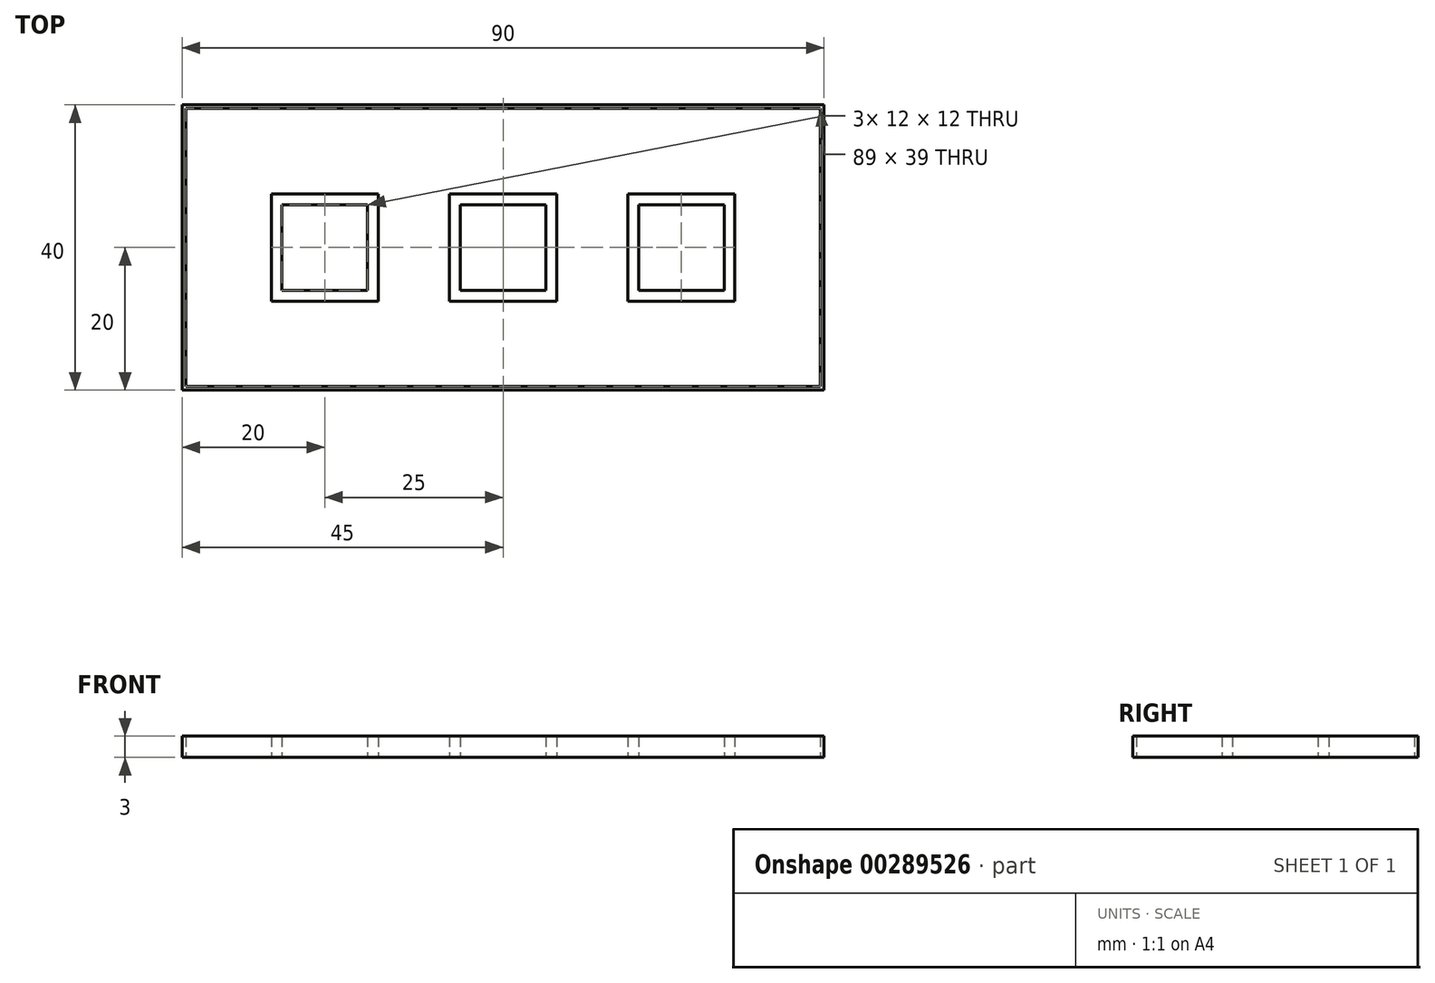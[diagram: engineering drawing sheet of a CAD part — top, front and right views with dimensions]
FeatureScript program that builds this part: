
annotation { "Feature Type Name" : "Feature", "Feature Type Description" : "" }
export const myFeature = defineFeature(function(context is Context, id is Id, definition is map)
    precondition{}
    {
        {
            var Q0;
            Q0=qCreatedBy(makeId("Top.planeOp"),FACE);
            var sketch = newSketch(context, id + "F0", { "sketchPlane" : qUnion([Q0])});
            skLineSegment(sketch, "E0.bottom", {"start": v(7.5, 7.5) * mm, "end": v(-7.5, 7.5) * mm});
            skLineSegment(sketch, "E0.top", {"start": v(7.5, -7.5) * mm, "end": v(-7.5, -7.5) * mm});
            skLineSegment(sketch, "E0.left", {"start": v(7.5, 7.5) * mm, "end": v(7.5, -7.5) * mm});
            skLineSegment(sketch, "E0.right", {"start": v(-7.5, 7.5) * mm, "end": v(-7.5, -7.5) * mm});
            skPoint(sketch, "E0.middle", {"position": v(0, 0) * mm});
            skLineSegment(sketch, "E1.bottom", {"start": v(-6, 6) * mm, "end": v(6, 6) * mm});
            skLineSegment(sketch, "E1.top", {"start": v(-6, -6) * mm, "end": v(6, -6) * mm});
            skLineSegment(sketch, "E1.left", {"start": v(-6, 6) * mm, "end": v(-6, -6) * mm});
            skLineSegment(sketch, "E1.right", {"start": v(6, 6) * mm, "end": v(6, -6) * mm});
            skLineSegment(sketch, "E2.bottom", {"start": v(17.5, 7.5) * mm, "end": v(32.5, 7.5) * mm});
            skLineSegment(sketch, "E2.top", {"start": v(17.5, -7.5) * mm, "end": v(32.5, -7.5) * mm});
            skLineSegment(sketch, "E2.left", {"start": v(17.5, 7.5) * mm, "end": v(17.5, -7.5) * mm});
            skLineSegment(sketch, "E2.right", {"start": v(32.5, 7.5) * mm, "end": v(32.5, -7.5) * mm});
            skPoint(sketch, "E2.middle", {"position": v(25, 0) * mm});
            skLineSegment(sketch, "E3.bottom", {"start": v(-32.5, 7.5) * mm, "end": v(-17.5, 7.5) * mm});
            skLineSegment(sketch, "E3.top", {"start": v(-32.5, -7.5) * mm, "end": v(-17.5, -7.5) * mm});
            skLineSegment(sketch, "E3.left", {"start": v(-32.5, 7.5) * mm, "end": v(-32.5, -7.5) * mm});
            skLineSegment(sketch, "E3.right", {"start": v(-17.5, 7.5) * mm, "end": v(-17.5, -7.5) * mm});
            skPoint(sketch, "E3.middle", {"position": v(-25, 0) * mm});
            skLineSegment(sketch, "E4.bottom", {"start": v(-31, 6) * mm, "end": v(-19, 6) * mm});
            skLineSegment(sketch, "E4.top", {"start": v(-31, -6) * mm, "end": v(-19, -6) * mm});
            skLineSegment(sketch, "E4.left", {"start": v(-31, 6) * mm, "end": v(-31, -6) * mm});
            skLineSegment(sketch, "E4.right", {"start": v(-19, 6) * mm, "end": v(-19, -6) * mm});
            skLineSegment(sketch, "E5.bottom", {"start": v(31, 6) * mm, "end": v(19, 6) * mm});
            skLineSegment(sketch, "E5.top", {"start": v(31, -6) * mm, "end": v(19, -6) * mm});
            skLineSegment(sketch, "E5.left", {"start": v(31, 6) * mm, "end": v(31, -6) * mm});
            skLineSegment(sketch, "E5.right", {"start": v(19, 6) * mm, "end": v(19, -6) * mm});
            skLineSegment(sketch, "E6.bottom", {"start": v(45, 20) * mm, "end": v(-45, 20) * mm});
            skLineSegment(sketch, "E6.top", {"start": v(45, -20) * mm, "end": v(-45, -20) * mm});
            skLineSegment(sketch, "E6.left", {"start": v(45, 20) * mm, "end": v(45, -20) * mm});
            skLineSegment(sketch, "E6.right", {"start": v(-45, 20) * mm, "end": v(-45, -20) * mm});
            skLineSegment(sketch, "E7.bottom", {"start": v(44.5, 19.5) * mm, "end": v(-44.5, 19.5) * mm});
            skLineSegment(sketch, "E7.top", {"start": v(44.5, -19.5) * mm, "end": v(-44.5, -19.5) * mm});
            skLineSegment(sketch, "E7.left", {"start": v(44.5, 19.5) * mm, "end": v(44.5, -19.5) * mm});
            skLineSegment(sketch, "E7.right", {"start": v(-44.5, 19.5) * mm, "end": v(-44.5, -19.5) * mm});
            skSolve(sketch);
        }
        {
            var Q0;
            Q0=makeQuery(id+"F0.imprint","IMPRINT",FACE,{"disambiguationData":[TD([[makeQuery(id+"F0.imprint","IMPRINT",EDGE,{"derivedFrom":sQuery(id+"F0.wireOp",EDGE,"E0.bottom")}),1.0]])]});
            var Q1;
            Q1=makeQuery(id+"F0.imprint","IMPRINT",FACE,{"disambiguationData":[TD([[makeQuery(id+"F0.imprint","IMPRINT",EDGE,{"derivedFrom":sQuery(id+"F0.wireOp",EDGE,"E2.bottom")}),-1.0]])]});
            var Q2;
            Q2=makeQuery(id+"F0.imprint","IMPRINT",FACE,{"disambiguationData":[TD([[makeQuery(id+"F0.imprint","IMPRINT",EDGE,{"derivedFrom":sQuery(id+"F0.wireOp",EDGE,"E3.bottom")}),-1.0]])]});
            extrude(context, id + "F1", {"entities" : qUnion([Q0, Q1, Q2]), "depth" : 3 * mm});
        }
        {
            var Q0;
            Q0 = qSketchRegion(id + "F0", true);
            extrude(context, id + "F2", {"entities" : qUnion([Q0]), "depth" : 3 * mm});
        }
    });
